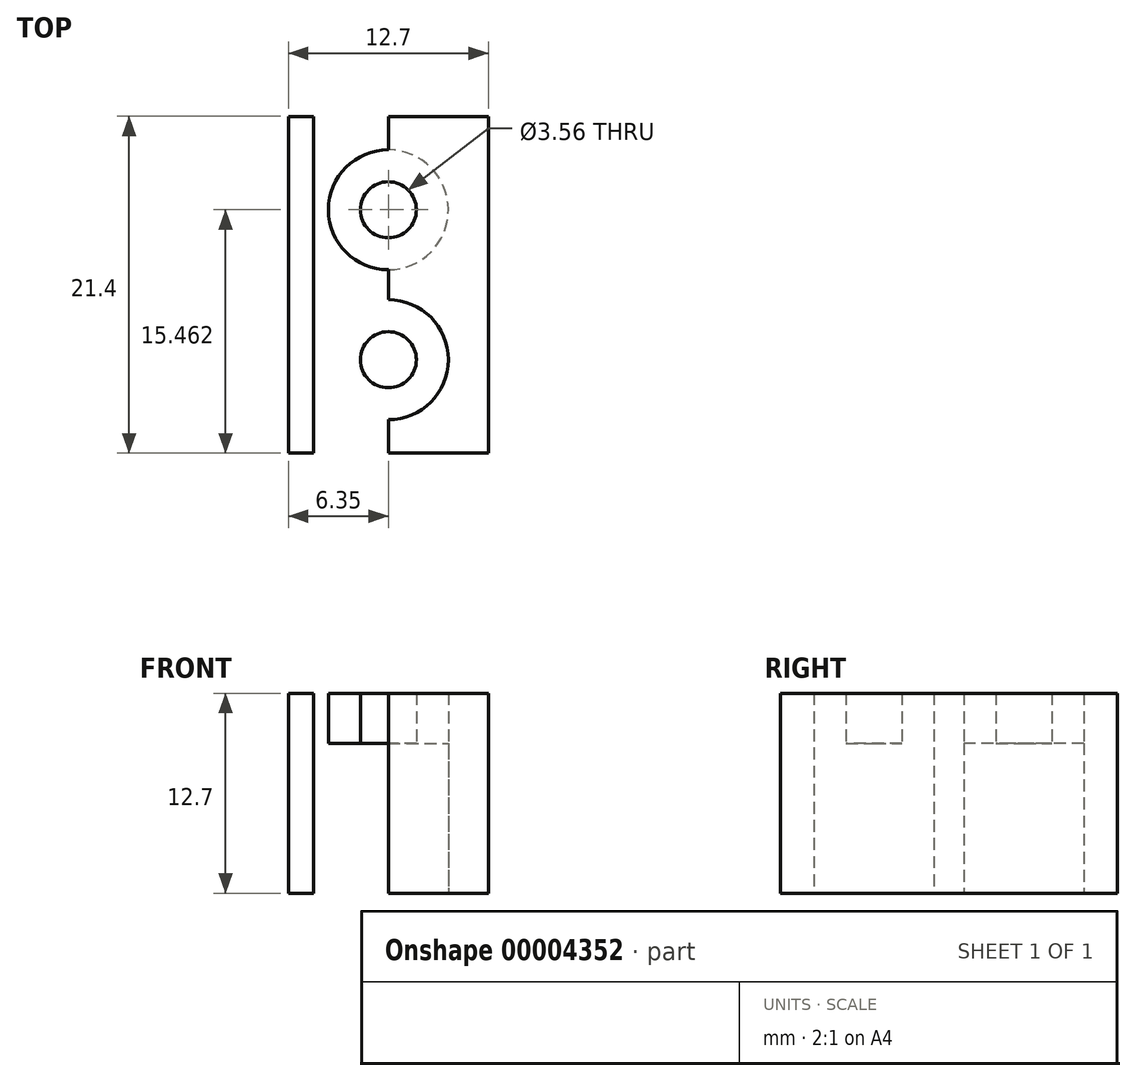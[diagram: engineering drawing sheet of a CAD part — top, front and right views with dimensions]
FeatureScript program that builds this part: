
annotation { "Feature Type Name" : "Feature", "Feature Type Description" : "" }
export const myFeature = defineFeature(function(context is Context, id is Id, definition is map)
    precondition{}
    {
        {
            var Q0;
            Q0=qCreatedBy(makeId("Top.planeOp"),FACE);
            var sketch = newSketch(context, id + "F0", { "sketchPlane" : qUnion([Q0])});
            skLineSegment(sketch, "E0.rect.bottom", {"start": v(6.35, -10.7) * mm, "end": v(-6.35, -10.7) * mm});
            skLineSegment(sketch, "E0.rect.top", {"start": v(6.35, 10.7) * mm, "end": v(-6.35, 10.7) * mm});
            skLineSegment(sketch, "E0.rect.left", {"start": v(6.35, -10.7) * mm, "end": v(6.35, 10.7) * mm});
            skLineSegment(sketch, "E0.rect.right", {"start": v(-6.35, -10.7) * mm, "end": v(-6.35, 10.7) * mm});
            skPoint(sketch, "E0.rect.middle", {"position": v(0, 0) * mm});
            skCircle(sketch, "E1", {"center": v(0, 4.76) * mm, "radius": 1.78 * mm});
            skLineSegment(sketch, "E2", {"start": v(-6.35, 0) * mm, "end": v(6.35, 0) * mm, "construction": true});
            skCircle(sketch, "E3.0.MirrorC", {"center": v(0, -4.76) * mm, "radius": 1.78 * mm});
            skLineSegment(sketch, "E4.bottom", {"start": v(0, 10.7) * mm, "end": v(-4.76, 10.7) * mm});
            skLineSegment(sketch, "E4.top", {"start": v(0, -10.7) * mm, "end": v(-4.76, -10.7) * mm});
            skLineSegment(sketch, "E4.left", {"start": v(0, 10.7) * mm, "end": v(0, -10.7) * mm});
            skLineSegment(sketch, "E4.right", {"start": v(-4.76, 10.7) * mm, "end": v(-4.76, -10.7) * mm});
            skCircle(sketch, "E5", {"center": v(0, -4.76) * mm, "radius": 3.81 * mm});
            skCircle(sketch, "E6", {"center": v(0, 4.76) * mm, "radius": 3.81 * mm});
            skSolve(sketch);
        }
        {
            var Q0;
            {var subQ11=sQuery(id+"F0.wireOp",EDGE,"E0.rect.left");Q0=makeQuery(id+"F0.imprint","IMPRINT",FACE,{"disambiguationData":[TD([[makeQuery(id+"F0.imprint","IMPRINT",EDGE,{"derivedFrom":subQ11}),1.0]])]});}
            var Q1;
            {var subQ8=sQuery(id+"F0.wireOp",EDGE,"E4.bottom");Q1=makeQuery(id+"F0.imprint","IMPRINT",FACE,{"disambiguationData":[TD([[makeQuery(id+"F0.imprint","IMPRINT",EDGE,{"derivedFrom":subQ8}),1.0]])]});}
            var Q2;
            {var subQ1=sQuery(id+"F0.wireOp",EDGE,"E0.rect.right");Q2=makeQuery(id+"F0.imprint","IMPRINT",FACE,{"disambiguationData":[TD([[makeQuery(id+"F0.imprint","IMPRINT",EDGE,{"derivedFrom":subQ1}),-1.0]])]});}
            var Q3;
            {var subQ1=sQuery(id+"F0.wireOp",EDGE,"E4.left");var subQ4=sQuery(id+"F0.wireOp",EDGE,"E3.0.MirrorC");var subQ6=makeQuery(id+"F0.imprint","INTERSECT",VERTEX,{"disambiguationData":[OD(0.0)],"derivedFrom":[subQ4,subQ1]});Q3=makeQuery(id+"F0.imprint","IMPRINT",FACE,{"disambiguationData":[TD([[makeQuery(id+"F0.imprint","IMPRINT",EDGE,{"disambiguationData":[TD([[subQ6,-1.0]])],"derivedFrom":subQ4}),1.0]])]});}
            var Q4;
            {var subQ0=sQuery(id+"F0.wireOp",EDGE,"E4.left");var subQ3=sQuery(id+"F0.wireOp",EDGE,"E3.0.MirrorC");var subQ6=makeQuery(id+"F0.imprint","INTERSECT",VERTEX,{"disambiguationData":[OD(0.0)],"derivedFrom":[subQ3,subQ0]});Q4=makeQuery(id+"F0.imprint","IMPRINT",FACE,{"disambiguationData":[TD([[makeQuery(id+"F0.imprint","IMPRINT",EDGE,{"disambiguationData":[TD([[subQ6,1.0]])],"derivedFrom":subQ3}),1.0]])]});}
            var Q5;
            {var subQ1=sQuery(id+"F0.wireOp",EDGE,"E4.left");var subQ4=sQuery(id+"F0.wireOp",EDGE,"E1");var subQ6=makeQuery(id+"F0.imprint","INTERSECT",VERTEX,{"disambiguationData":[OD(0.0)],"derivedFrom":[subQ4,subQ1]});Q5=makeQuery(id+"F0.imprint","IMPRINT",FACE,{"disambiguationData":[TD([[makeQuery(id+"F0.imprint","IMPRINT",EDGE,{"disambiguationData":[TD([[subQ6,-1.0]])],"derivedFrom":subQ4}),-1.0]])]});}
            var Q6;
            {var subQ1=sQuery(id+"F0.wireOp",EDGE,"E4.left");var subQ4=sQuery(id+"F0.wireOp",EDGE,"E1");var subQ6=makeQuery(id+"F0.imprint","INTERSECT",VERTEX,{"disambiguationData":[OD(0.0)],"derivedFrom":[subQ4,subQ1]});Q6=makeQuery(id+"F0.imprint","IMPRINT",FACE,{"disambiguationData":[TD([[makeQuery(id+"F0.imprint","IMPRINT",EDGE,{"disambiguationData":[TD([[subQ6,1.0]])],"derivedFrom":subQ4}),-1.0]])]});}
            extrude(context, id + "F1", {"entities" : qUnion([Q0, Q1, Q2, Q3, Q4, Q5, Q6]), "depth" : 12.7 * mm});
        }
        {
            var Q0;
            {var subQ8=sQuery(id+"F0.wireOp",EDGE,"E4.bottom");Q0=makeQuery(id+"F0.imprint","IMPRINT",FACE,{"disambiguationData":[TD([[makeQuery(id+"F0.imprint","IMPRINT",EDGE,{"derivedFrom":subQ8}),1.0]])]});}
            var Q1;
            {var subQ1=sQuery(id+"F0.wireOp",EDGE,"E4.left");var subQ4=sQuery(id+"F0.wireOp",EDGE,"E1");var subQ6=makeQuery(id+"F0.imprint","INTERSECT",VERTEX,{"disambiguationData":[OD(0.0)],"derivedFrom":[subQ4,subQ1]});Q1=makeQuery(id+"F0.imprint","IMPRINT",FACE,{"disambiguationData":[TD([[makeQuery(id+"F0.imprint","IMPRINT",EDGE,{"disambiguationData":[TD([[subQ6,-1.0]])],"derivedFrom":subQ4}),-1.0]])]});}
            var Q2;
            {var subQ0=sQuery(id+"F0.wireOp",EDGE,"E4.left");var subQ3=sQuery(id+"F0.wireOp",EDGE,"E3.0.MirrorC");var subQ6=makeQuery(id+"F0.imprint","INTERSECT",VERTEX,{"disambiguationData":[OD(0.0)],"derivedFrom":[subQ3,subQ0]});Q2=makeQuery(id+"F0.imprint","IMPRINT",FACE,{"disambiguationData":[TD([[makeQuery(id+"F0.imprint","IMPRINT",EDGE,{"disambiguationData":[TD([[subQ6,1.0]])],"derivedFrom":subQ3}),1.0]])]});}
            var Q3;
            {var subQ0=sQuery(id+"F0.wireOp",EDGE,"E4.left");var subQ1=sQuery(id+"F0.wireOp",EDGE,"E3.0.MirrorC");var subQ3=makeQuery(id+"F0.imprint","INTERSECT",VERTEX,{"disambiguationData":[OD(0.0)],"derivedFrom":[subQ1,subQ0]});Q3=makeQuery(id+"F0.imprint","IMPRINT",FACE,{"disambiguationData":[TD([[makeQuery(id+"F0.imprint","IMPRINT",EDGE,{"disambiguationData":[TD([[subQ3,1.0]])],"derivedFrom":subQ1}),-1.0]])]});}
            var Q4;
            {var subQ0=sQuery(id+"F0.wireOp",EDGE,"E4.left");var subQ1=sQuery(id+"F0.wireOp",EDGE,"E1");var subQ3=makeQuery(id+"F0.imprint","INTERSECT",VERTEX,{"disambiguationData":[OD(0.0)],"derivedFrom":[subQ1,subQ0]});Q4=makeQuery(id+"F0.imprint","IMPRINT",FACE,{"disambiguationData":[TD([[makeQuery(id+"F0.imprint","IMPRINT",EDGE,{"disambiguationData":[TD([[subQ3,-1.0]])],"derivedFrom":subQ1}),1.0]])]});}
            var Q5;
            Q5=sQuery(id+"F0.wireOp",EDGE,"E4.left");
            revolve(context, id + "F2", {"operationType" : NewBodyOperationType.REMOVE, "entities" : qUnion([Q0, Q1, Q2, Q3, Q4]), "axis" : qUnion([Q5]), "revolveType" : RevolveType.FULL, "oppositeDirection" : true});
        }
        {
            var Q0;
            {var subQ1=sQuery(id+"F0.wireOp",EDGE,"E4.left");var subQ4=sQuery(id+"F0.wireOp",EDGE,"E3.0.MirrorC");var subQ6=makeQuery(id+"F0.imprint","INTERSECT",VERTEX,{"disambiguationData":[OD(0.0)],"derivedFrom":[subQ4,subQ1]});Q0=makeQuery(id+"F0.imprint","IMPRINT",FACE,{"disambiguationData":[TD([[makeQuery(id+"F0.imprint","IMPRINT",EDGE,{"disambiguationData":[TD([[subQ6,-1.0]])],"derivedFrom":subQ4}),1.0]])]});}
            var Q1;
            {var subQ0=sQuery(id+"F0.wireOp",EDGE,"E4.left");var subQ3=sQuery(id+"F0.wireOp",EDGE,"E3.0.MirrorC");var subQ6=makeQuery(id+"F0.imprint","INTERSECT",VERTEX,{"disambiguationData":[OD(0.0)],"derivedFrom":[subQ3,subQ0]});Q1=makeQuery(id+"F0.imprint","IMPRINT",FACE,{"disambiguationData":[TD([[makeQuery(id+"F0.imprint","IMPRINT",EDGE,{"disambiguationData":[TD([[subQ6,1.0]])],"derivedFrom":subQ3}),1.0]])]});}
            var Q2;
            {var subQ1=sQuery(id+"F0.wireOp",EDGE,"E4.left");var subQ4=sQuery(id+"F0.wireOp",EDGE,"E1");var subQ6=makeQuery(id+"F0.imprint","INTERSECT",VERTEX,{"disambiguationData":[OD(0.0)],"derivedFrom":[subQ4,subQ1]});Q2=makeQuery(id+"F0.imprint","IMPRINT",FACE,{"disambiguationData":[TD([[makeQuery(id+"F0.imprint","IMPRINT",EDGE,{"disambiguationData":[TD([[subQ6,-1.0]])],"derivedFrom":subQ4}),-1.0]])]});}
            var Q3;
            {var subQ1=sQuery(id+"F0.wireOp",EDGE,"E4.left");var subQ4=sQuery(id+"F0.wireOp",EDGE,"E1");var subQ6=makeQuery(id+"F0.imprint","INTERSECT",VERTEX,{"disambiguationData":[OD(0.0)],"derivedFrom":[subQ4,subQ1]});Q3=makeQuery(id+"F0.imprint","IMPRINT",FACE,{"disambiguationData":[TD([[makeQuery(id+"F0.imprint","IMPRINT",EDGE,{"disambiguationData":[TD([[subQ6,1.0]])],"derivedFrom":subQ4}),-1.0]])]});}
            extrude(context, id + "F3", {"entities" : qUnion([Q0, Q1, Q2, Q3]), "operationType" : NewBodyOperationType.REMOVE, "depth" : 9.52 * mm});
        }
    });
